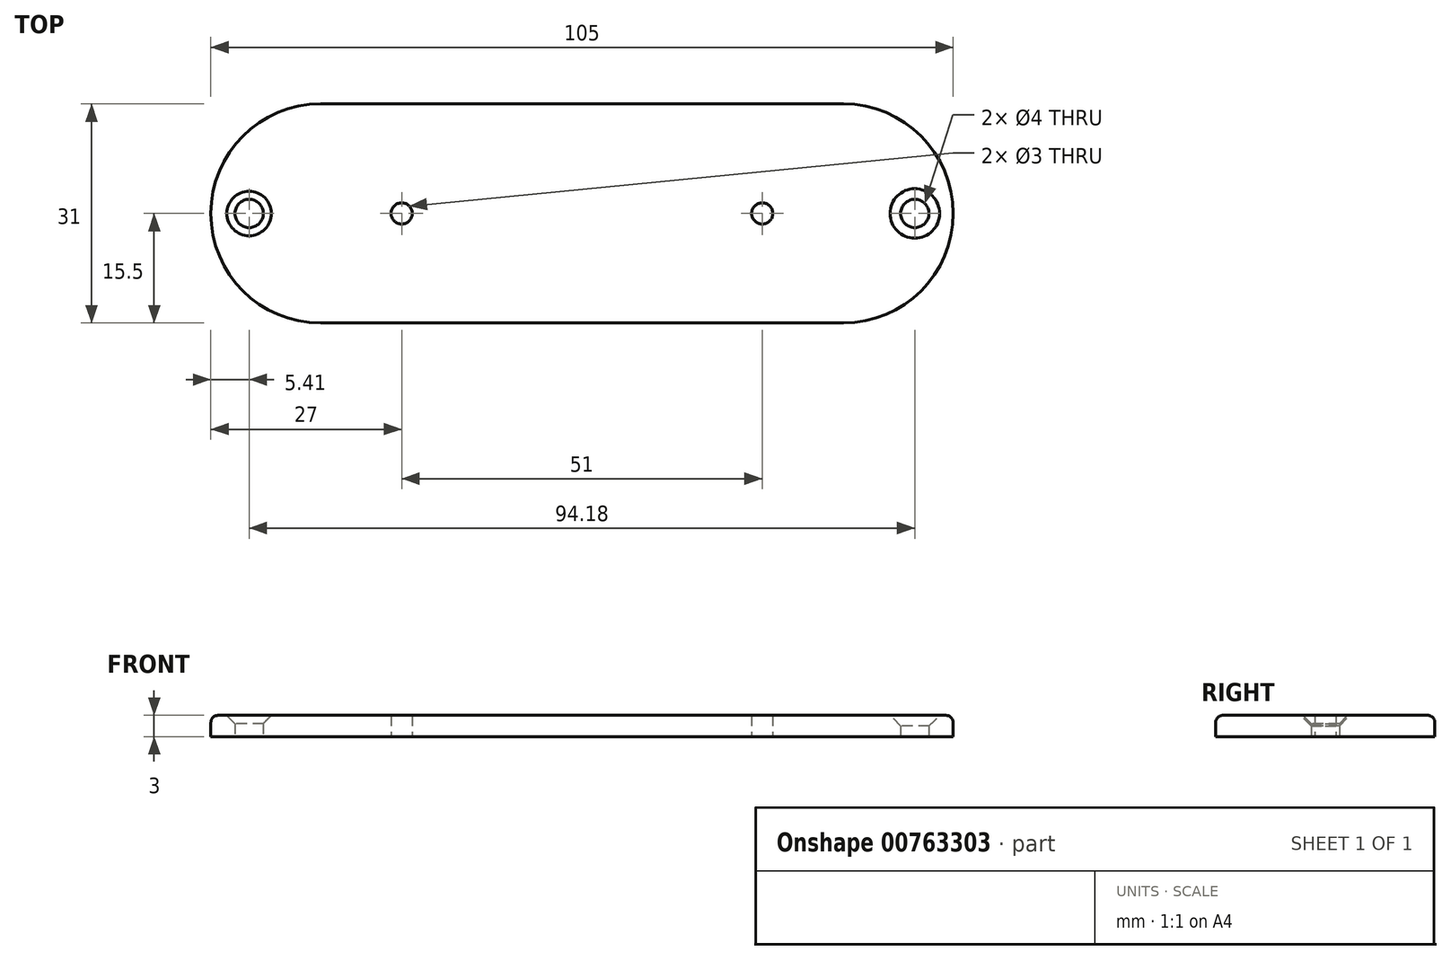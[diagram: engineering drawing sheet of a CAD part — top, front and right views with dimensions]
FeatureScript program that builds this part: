
annotation { "Feature Type Name" : "Feature", "Feature Type Description" : "" }
export const myFeature = defineFeature(function(context is Context, id is Id, definition is map)
    precondition{}
    {
        {
            var Q0;
            Q0=qCreatedBy(makeId("Top.planeOp"),FACE);
            var sketch = newSketch(context, id + "F0", { "sketchPlane" : qUnion([Q0])});
            skLineSegment(sketch, "E0.bottom", {"start": v(0, 0) * mm, "end": v(-74, 0) * mm});
            skLineSegment(sketch, "E0.top", {"start": v(0, 31) * mm, "end": v(-74, 31) * mm});
            skArc(sketch, "E1", {"start": v(-74, 0) * mm, "mid": v(-89.5, 15.5) * mm, "end": v(-74, 31) * mm});
            skArc(sketch, "E2", {"start": v(0, 31) * mm, "mid": v(15.5, 15.5) * mm, "end": v(0, 0) * mm});
            skCircle(sketch, "E3", {"center": v(-84.1, 15.5) * mm, "radius": 2 * mm});
            skCircle(sketch, "E4", {"center": v(-62.5, 15.5) * mm, "radius": 1.5 * mm});
            skCircle(sketch, "E5", {"center": v(-11.5, 15.5) * mm, "radius": 1.5 * mm});
            skCircle(sketch, "E6", {"center": v(10.09, 15.5) * mm, "radius": 2 * mm});
            skSolve(sketch);
        }
        {
            var Q0;
            Q0=makeQuery(id+"F0.imprint","IMPRINT",FACE,{"disambiguationData":[TD([[makeQuery(id+"F0.imprint","IMPRINT",EDGE,{"derivedFrom":sQuery(id+"F0.wireOp",EDGE,"E0.bottom")}),-1.0]])]});
            extrude(context, id + "F1", {"entities" : qUnion([Q0]), "depth" : 3 * mm, "offsetDistance" : 25 * mm});
        }
        {
            var Q0;
            Q0=makeQuery(id+"F1.opExtrude","CAP_EDGE",EDGE,{"disambiguationData":[OSD([sQuery(id+"F0.wireOp",EDGE,"E1")])],"isStart":false});
            var Q1;
            Q1=makeQuery(id+"F1.opExtrude","CAP_EDGE",EDGE,{"disambiguationData":[OSD([sQuery(id+"F0.wireOp",EDGE,"E0.bottom")])],"isStart":false});
            var Q2;
            Q2=makeQuery(id+"F1.opExtrude","CAP_EDGE",EDGE,{"disambiguationData":[OSD([sQuery(id+"F0.wireOp",EDGE,"E0.top")])],"isStart":false});
            var Q3;
            Q3=makeQuery(id+"F1.opExtrude","CAP_EDGE",EDGE,{"disambiguationData":[OSD([sQuery(id+"F0.wireOp",EDGE,"E2")])],"isStart":false});
            fillet(context, id + "F2", {"entities" : qUnion([Q0, Q1, Q2, Q3]), "radius" : 1 * mm, "tangentPropagation" : true, "allowEdgeOverflow" : false});
        }
        {
            var Q0;
            Q0=makeQuery(id+"F1.opExtrude","CAP_EDGE",EDGE,{"disambiguationData":[OSD([sQuery(id+"F0.wireOp",EDGE,"E3")])],"isStart":false});
            chamfer(context, id + "F3", {"entities" : qUnion([Q0]), "width" : 1.15 * mm, "tangentPropagation" : true});
        }
        {
            var Q0;
            Q0=makeQuery(id+"F1.opExtrude","CAP_EDGE",EDGE,{"disambiguationData":[OSD([sQuery(id+"F0.wireOp",EDGE,"E6")])],"isStart":false});
            chamfer(context, id + "F4", {"entities" : qUnion([Q0]), "width" : 1.5 * mm, "tangentPropagation" : true});
        }
    });
